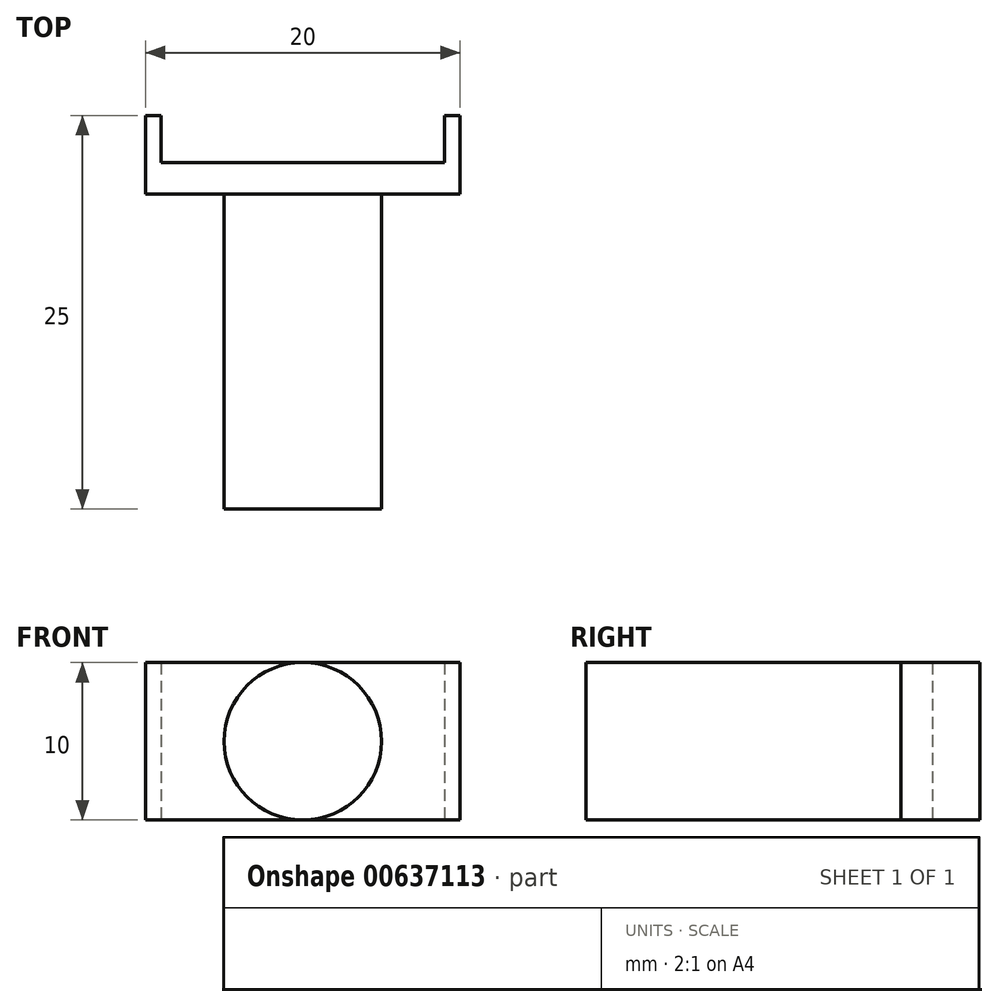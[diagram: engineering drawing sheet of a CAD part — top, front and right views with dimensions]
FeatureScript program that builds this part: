
annotation { "Feature Type Name" : "Feature", "Feature Type Description" : "" }
export const myFeature = defineFeature(function(context is Context, id is Id, definition is map)
    precondition{}
    {
        {
            var Q0;
            Q0=qCreatedBy(makeId("Top.planeOp"),FACE);
            var sketch = newSketch(context, id + "F0", { "sketchPlane" : qUnion([Q0])});
            skLineSegment(sketch, "E0.bottom", {"start": v(5, 10) * mm, "end": v(-5, 10) * mm});
            skLineSegment(sketch, "E0.top", {"start": v(5, -10) * mm, "end": v(-5, -10) * mm});
            skLineSegment(sketch, "E0.left", {"start": v(5, 10) * mm, "end": v(5, -10) * mm});
            skLineSegment(sketch, "E0.right", {"start": v(-5, 10) * mm, "end": v(-5, -10) * mm});
            skPoint(sketch, "E0.middle", {"position": v(0, 0) * mm});
            skLineSegment(sketch, "E1", {"start": v(-5, 10) * mm, "end": v(-10, 10) * mm});
            skLineSegment(sketch, "E2", {"start": v(-10, 10) * mm, "end": v(-10, 15) * mm});
            skLineSegment(sketch, "E3", {"start": v(-10, 15) * mm, "end": v(-9, 15) * mm});
            skLineSegment(sketch, "E4", {"start": v(-9, 15) * mm, "end": v(-9, 12) * mm});
            skLineSegment(sketch, "E5", {"start": v(-9, 12) * mm, "end": v(9, 12) * mm});
            skLineSegment(sketch, "E6", {"start": v(10, 10) * mm, "end": v(5, 10) * mm});
            skLineSegment(sketch, "E7", {"start": v(9, 12) * mm, "end": v(9, 15) * mm});
            skLineSegment(sketch, "E8", {"start": v(10, 10) * mm, "end": v(10, 15) * mm});
            skLineSegment(sketch, "E9", {"start": v(10, 15) * mm, "end": v(9, 15) * mm});
            skLineSegment(sketch, "E10", {"start": v(0, 10) * mm, "end": v(0, -10) * mm});
            skSolve(sketch);
        }
        {
            var Q0;
            Q0=makeQuery(id+"F0.imprint","IMPRINT",FACE,{"disambiguationData":[TD([[makeQuery(id+"F0.imprint","IMPRINT",EDGE,{"derivedFrom":sQuery(id+"F0.wireOp",EDGE,"E0.bottom")}),-1.0]])]});
            extrude(context, id + "F1", {"entities" : qUnion([Q0]), "endBound" : BoundingType.SYMMETRIC, "depth" : 10 * mm, "offsetDistance" : 25 * mm});
        }
        {
            var Q0;
            {var subQ0=sQuery(id+"F0.wireOp",EDGE,"E0.right");Q0=makeQuery(id+"F0.imprint","IMPRINT",FACE,{"disambiguationData":[TD([[makeQuery(id+"F0.imprint","IMPRINT",EDGE,{"derivedFrom":subQ0}),1.0]])]});}
            var Q1;
            Q1=sQuery(id+"F0.wireOp",EDGE,"E10");
            revolve(context, id + "F2", {"operationType" : NewBodyOperationType.ADD, "entities" : qUnion([Q0]), "axis" : qUnion([Q1]), "revolveType" : RevolveType.FULL});
        }
    });
